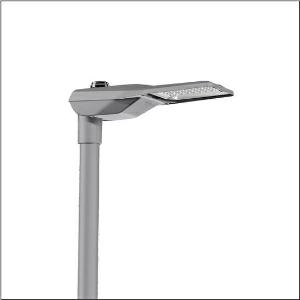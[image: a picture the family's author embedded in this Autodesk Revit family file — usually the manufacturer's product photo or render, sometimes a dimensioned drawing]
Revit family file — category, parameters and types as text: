
# Revit family: streetlight_sl_21_mini___p0_8a_5xe6u57n08hb_6fdb
name_source: partatom
category: Lighting Fixtures
units: mm (PartAtom-declared; Revit-internal decimal feet)

## family parameters
Cut with Voids When Loaded = No
Host = Face
Light Source = No
Part Type = Normal
Room Calculation Point = No
Round Connector Dimension = Use Diameter
Shared = No

## types (1)
- --- (1 x LED, 7850 lm, 66 W, 3000K)
    Apparent Load = 66 VA
    CIE Flux Codes = 33 69 96 100 100
    Color Rendering = 80
    Color Temperature = 3000K
    Default Elevation = 1800 mm
    Description = Streetlight SL 21 mini, mast luminaire, primary light control with lens, of PMMA, primary optical cover: cover, of toughened safety glass, transparent, light distribution: P0.8a, light emission: direct distribution, primary light characteristic: asymmetric, installation type: side-entry, LED, 3G 1.5mm², High Power LED, rated luminous flux: 7.850lm, luminous efficacy: 119lm/W, light colour: 830, colour temperature: 3000K, control gear: NEMA (7pin), control: flexible luminous flux parameterisation, time-dependent luminous flux control, constant luminous flux control, pre-setting: linear dimming characteristic, overheat protection, mains connection: 230..240V, AC, 50/60Hz, connection cable pre-assembled, cable length: 8,5m, wiring characteristics: H07RN-F, start of lifetime: 66W, end of service life: 69W, reduction: 30W, luminaire housing, of diecast aluminium (EN AC-44300), powder-coated, SITECO metallic grey (DB 702S), corrosivity category C5 high according to DIN EN ISO 12944, multi-level sealing system, sealing non-destructively replaceable, inclination adjustable: 0°, 5°, 10°, 15°, length: 628mm, width: 235mm, height: 110mm, spigot size: 42mm (side-entry), mounting height: 4..8m, protection rating (complete): IP66, insulation class (complete): insulation class I (protective earthing), certification: CE, ENEC, ENEC+, VDE, impact resistance: IK10, permissible operating ambient temperature for outdoor applications: -40..+50°C, standard-compliant lighting for roads and squares, packaging unit: 1 piece

Light Distribution: P0.8a
    Height = 110 mm
    Lamp = 1 x LED
    Lamp Light Flux = 7850 lm
    Lamp Power = 66 W
    Lamp count = 1
    Length = 625 mm
    Luminous efficacy = 119 lm/W
    Manufacturer = Siteco
    ModVariant = No
    Model = 5XE6U57N08HB
    Mounting Place = Pole
    Mounting Type = Pole top
    Number of Poles = 1
    OnlyDefault = Yes
    Power Factor = 1
    Product Name = Streetlight SL 21 mini | P0.8a
    Product group = mast luminaire | pylon top
    ProductGroupID = 6100
    Protection Class = Protection class I
    Protection Degree = IP 66
    RLX_Detail_Level = 1
    RLX_Emergency_Light_Flux = 0 lm
    RLX_Emergency_Type = 0
    RLX_Emergency_Type_DB = No
    RlxData = <blob elided: 91669 chars, md5=b58967c4>
    Socket = socket
    Standby Power = 0 W
    System Light Flux = 7850 lm
    System Power = 66 W
    Type Comments = factory setting: luminous flux: 100 % | dim-lin: 254 | 670 mA
    Type Image = l_1294379.jpg
    URL = http://relux.com
    VarID = @adj_082767
    Voltage = 0 V
    Weight = 0.00 kg
    Width = 234 mm

## geometry (parser evidence)
native form markers: Blend x4, Sweep x10
no freeform markers — native parametric forms only
